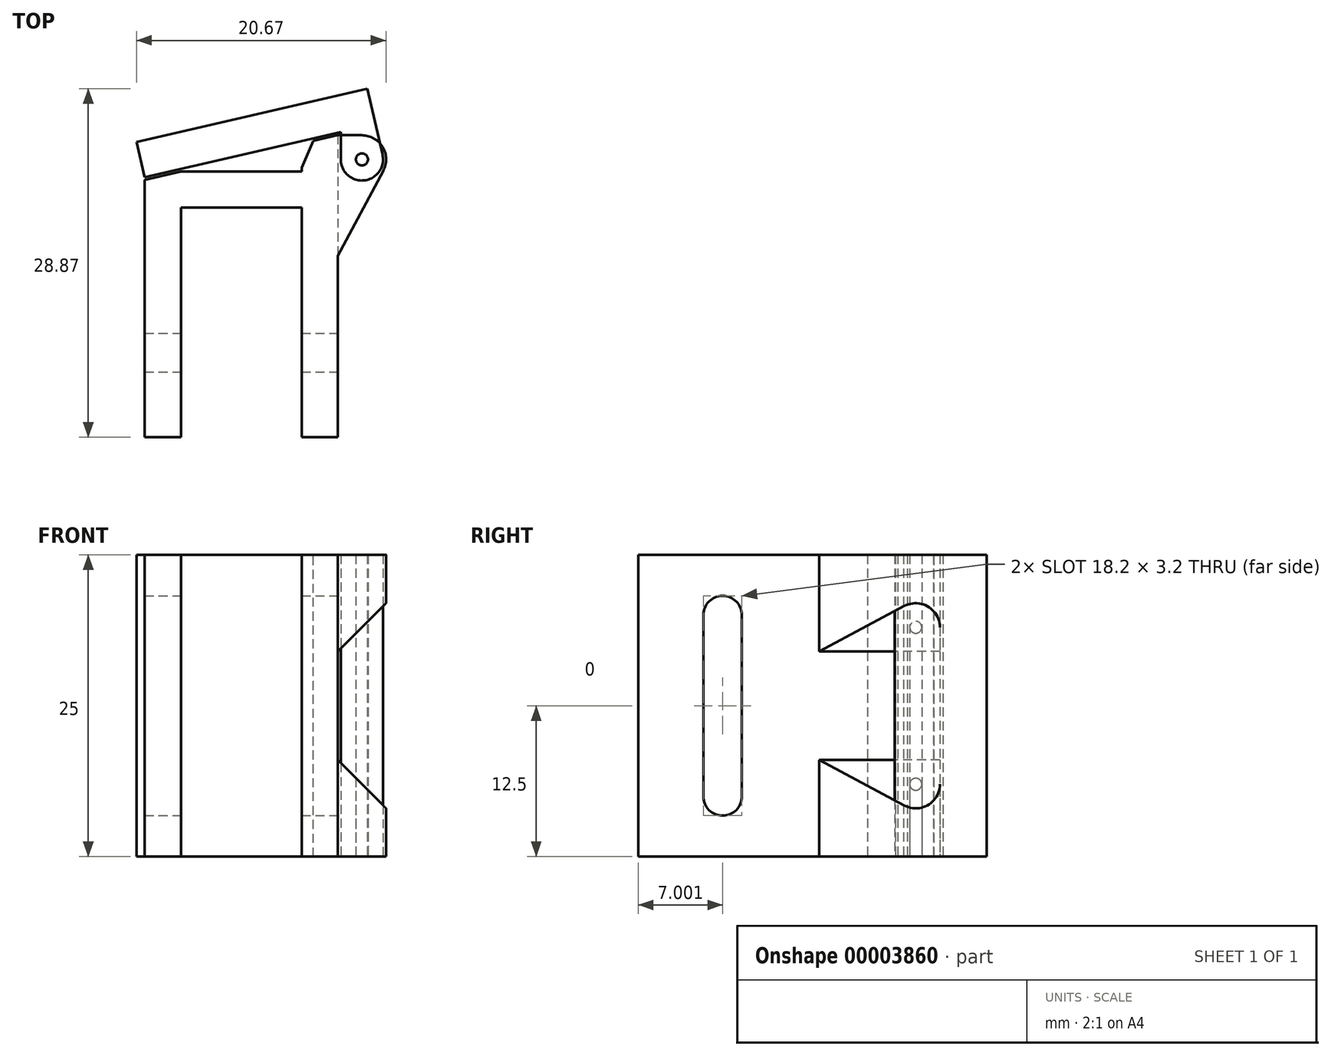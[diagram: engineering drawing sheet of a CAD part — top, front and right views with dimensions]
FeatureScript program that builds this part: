
annotation { "Feature Type Name" : "Feature", "Feature Type Description" : "" }
export const myFeature = defineFeature(function(context is Context, id is Id, definition is map)
    precondition{}
    {
        {
            var Q0;
            Q0=qCreatedBy(makeId("Top.planeOp"),FACE);
            var sketch = newSketch(context, id + "F0", { "sketchPlane" : qUnion([Q0])});
            skLineSegment(sketch, "E0", {"start": v(-92.53, 19.33) * mm, "end": v(-92.53, -5.67) * mm});
            skLineSegment(sketch, "E1", {"start": v(-92.53, -5.67) * mm, "end": v(-95.53, -5.67) * mm});
            skLineSegment(sketch, "E2", {"start": v(-95.53, -5.67) * mm, "end": v(-95.53, 13.33) * mm});
            skLineSegment(sketch, "E3", {"start": v(-95.53, 13.33) * mm, "end": v(-105.53, 13.33) * mm});
            skLineSegment(sketch, "E4", {"start": v(-105.53, 13.33) * mm, "end": v(-105.53, -5.67) * mm});
            skLineSegment(sketch, "E5", {"start": v(-105.53, -5.67) * mm, "end": v(-108.53, -5.67) * mm});
            skLineSegment(sketch, "E6", {"start": v(-108.53, -5.67) * mm, "end": v(-108.53, 15.64) * mm});
            skLineSegment(sketch, "E7", {"start": v(-105.53, 16.33) * mm, "end": v(-95.53, 16.33) * mm});
            skLineSegment(sketch, "E8", {"start": v(-95.53, 16.33) * mm, "end": v(-95.53, 18.64) * mm});
            skLineSegment(sketch, "E9", {"start": v(-92.53, 19.33) * mm, "end": v(-95.53, 18.64) * mm, "construction": true});
            skLineSegment(sketch, "E10", {"start": v(-105.53, 16.33) * mm, "end": v(-108.53, 15.64) * mm, "construction": true});
            skLineSegment(sketch, "E11", {"start": v(-108.53, 15.64) * mm, "end": v(-105.53, 16.33) * mm});
            skLineSegment(sketch, "E12", {"start": v(-92.53, 19.33) * mm, "end": v(-95.53, 18.64) * mm});
            skSolve(sketch);
        }
        {
            var Q0;
            Q0=makeQuery(id+"F0.imprint","IMPRINT",FACE,{"disambiguationData":[TD([[makeQuery(id+"F0.imprint","IMPRINT",EDGE,{"derivedFrom":sQuery(id+"F0.wireOp",EDGE,"E0")}),-1.0]])]});
            extrude(context, id + "F1", {"entities" : qUnion([Q0]), "depth" : 25 * mm});
        }
        {
            var Q0;
            Q0=makeQuery(id+"F1.opExtrude","CAP_FACE",FACE,{"disambiguationData":[OSD([sQuery(id+"F0.wireOp",EDGE,"E0"),sQuery(id+"F0.wireOp",EDGE,"E1"),sQuery(id+"F0.wireOp",EDGE,"E2"),sQuery(id+"F0.wireOp",EDGE,"E3"),sQuery(id+"F0.wireOp",EDGE,"E4"),sQuery(id+"F0.wireOp",EDGE,"E5"),sQuery(id+"F0.wireOp",EDGE,"E6"),sQuery(id+"F0.wireOp",EDGE,"E7"),sQuery(id+"F0.wireOp",EDGE,"E8"),sQuery(id+"F0.wireOp",EDGE,"E11"),sQuery(id+"F0.wireOp",EDGE,"E12")])],"isStart":true});
            var sketch = newSketch(context, id + "F2", { "sketchPlane" : qUnion([Q0])});
            skCircle(sketch, "E13", {"center": v(-90.53, -17.33) * mm, "radius": 0.5 * mm});
            skArc(sketch, "E14", {"start": v(-90.53, -19.33) * mm, "mid": v(-88.81, -18.36) * mm, "end": v(-88.76, -16.39) * mm});
            skLineSegment(sketch, "E15", {"start": v(-92.53, -19.33) * mm, "end": v(-90.53, -19.33) * mm});
            skLineSegment(sketch, "E16", {"start": v(-92.53, -9.33) * mm, "end": v(-88.76, -16.39) * mm});
            skLineSegment(sketch, "E17", {"start": v(-92.53, -19.33) * mm, "end": v(-92.53, -9.33) * mm});
            skSolve(sketch);
        }
        {
            var Q0;
            Q0=makeQuery(id+"F2.imprint","IMPRINT",FACE,{"disambiguationData":[TD([[makeQuery(id+"F2.imprint","IMPRINT",EDGE,{"derivedFrom":sQuery(id+"F2.wireOp",EDGE,"E13")}),-1.0]])]});
            extrude(context, id + "F3", {"entities" : qUnion([Q0]), "operationType" : NewBodyOperationType.ADD, "oppositeDirection" : true, "depth" : 25 * mm});
        }
        {
            var Q0;
            Q0=makeQuery(id+"F1.opExtrude","SWEPT_FACE",FACE,{"disambiguationData":[OSD([sQuery(id+"F0.wireOp",EDGE,"E1")])]});
            var sketch = newSketch(context, id + "F4", { "sketchPlane" : qUnion([Q0])});
            skLineSegment(sketch, "E18", {"start": v(-92.53, 17) * mm, "end": v(-82.19, 27.34) * mm});
            skLineSegment(sketch, "E19", {"start": v(-82.19, 27.34) * mm, "end": v(-82.19, -2.34) * mm});
            skLineSegment(sketch, "E20", {"start": v(-82.19, -2.34) * mm, "end": v(-92.53, 8) * mm});
            skLineSegment(sketch, "E21", {"start": v(-92.53, 8) * mm, "end": v(-92.53, 17) * mm});
            skSolve(sketch);
        }
        {
            var Q0;
            Q0=makeQuery(id+"F4.imprint","IMPRINT",FACE,{"disambiguationData":[TD([[makeQuery(id+"F4.imprint","IMPRINT",EDGE,{"derivedFrom":sQuery(id+"F4.wireOp",EDGE,"E18")}),-1.0]])]});
            extrude(context, id + "F5", {"entities" : qUnion([Q0]), "operationType" : NewBodyOperationType.REMOVE, "oppositeDirection" : true, "depth" : 30 * mm});
        }
        {
            var Q0;
            Q0=makeQuery(id+"F5.boolean.opBoolean","MERGE",FACE,{"derivedFrom":[makeQuery(id+"F1.opExtrude","SWEPT_FACE",FACE,{"disambiguationData":[OSD([sQuery(id+"F0.wireOp",EDGE,"E0")])]}),makeQuery(id+"F5.opExtrude","SWEPT_FACE",FACE,{"disambiguationData":[OSD([sQuery(id+"F4.wireOp",EDGE,"E21")])]})]});
            var sketch = newSketch(context, id + "F6", { "sketchPlane" : qUnion([Q0])});
            skArc(sketch, "E22", {"start": v(2.93, 20) * mm, "mid": v(1.33, 21.6) * mm, "end": v(-0.27, 20) * mm});
            skArc(sketch, "E23", {"start": v(-0.27, 5) * mm, "mid": v(1.33, 3.4) * mm, "end": v(2.93, 5) * mm});
            skLineSegment(sketch, "E24.right", {"start": v(2.93, 20) * mm, "end": v(2.93, 5) * mm});
            skLineSegment(sketch, "E25.right", {"start": v(-0.27, 5) * mm, "end": v(-0.27, 20) * mm});
            skSolve(sketch);
        }
        {
            var Q0;
            Q0=makeQuery(id+"F6.imprint","IMPRINT",FACE,{"disambiguationData":[TD([[makeQuery(id+"F6.imprint","IMPRINT",EDGE,{"derivedFrom":sQuery(id+"F6.wireOp",EDGE,"E22")}),1.0]])]});
            extrude(context, id + "F7", {"entities" : qUnion([Q0]), "operationType" : NewBodyOperationType.REMOVE, "oppositeDirection" : true, "depth" : 25 * mm});
        }
        {
            var Q0;
            Q0=makeQuery(id+"F1.opExtrude","SWEPT_EDGE",EDGE,{"disambiguationData":[OSD([sQuery(id+"F0.wireOp",EDGE,"E8"),sQuery(id+"F0.wireOp",EDGE,"E12")])]});
            chamfer(context, id + "F8", {"entities" : qUnion([Q0]), "chamferType" : ChamferType.TWO_OFFSETS, "width1" : 2 * mm, "oppositeDirection" : false, "width2" : 1 * mm, "tangentPropagation" : true});
        }
        {
            var Q0;
            Q0=makeQuery(id+"F3.boolean.opBoolean","MERGE",FACE,{"derivedFrom":[makeQuery(id+"F1.opExtrude","CAP_FACE",FACE,{"disambiguationData":[OSD([sQuery(id+"F0.wireOp",EDGE,"E0"),sQuery(id+"F0.wireOp",EDGE,"E1"),sQuery(id+"F0.wireOp",EDGE,"E2"),sQuery(id+"F0.wireOp",EDGE,"E3"),sQuery(id+"F0.wireOp",EDGE,"E4"),sQuery(id+"F0.wireOp",EDGE,"E5"),sQuery(id+"F0.wireOp",EDGE,"E6"),sQuery(id+"F0.wireOp",EDGE,"E7"),sQuery(id+"F0.wireOp",EDGE,"E8"),sQuery(id+"F0.wireOp",EDGE,"E11"),sQuery(id+"F0.wireOp",EDGE,"E12")])],"isStart":true}),makeQuery(id+"F3.opExtrude","CAP_FACE",FACE,{"disambiguationData":[OSD([sQuery(id+"F2.wireOp",EDGE,"E13"),sQuery(id+"F2.wireOp",EDGE,"E14"),sQuery(id+"F2.wireOp",EDGE,"E15"),sQuery(id+"F2.wireOp",EDGE,"E16"),sQuery(id+"F2.wireOp",EDGE,"E17")])],"isStart":true})]});
            var sketch = newSketch(context, id + "F9", { "sketchPlane" : qUnion([Q0])});
            skCircle(sketch, "E26", {"center": v(-90.53, -17.33) * mm, "radius": 0.5 * mm});
            skCircle(sketch, "E27", {"center": v(-90.53, -17.33) * mm, "radius": 1.75 * mm});
            skLineSegment(sketch, "E28", {"start": v(-90.53, -17.33) * mm, "end": v(-80.71, -17.33) * mm, "construction": true});
            skLineSegment(sketch, "E29", {"start": v(-90.53, -17.33) * mm, "end": v(-93.59, -17.33) * mm, "construction": true});
            skLineSegment(sketch, "E30", {"start": v(-92.28, -17.33) * mm, "end": v(-92.28, -19.6) * mm});
            skLineSegment(sketch, "E31", {"start": v(-92.28, -19.6) * mm, "end": v(-108.53, -15.84) * mm});
            skLineSegment(sketch, "E32", {"start": v(-108.53, -15.84) * mm, "end": v(-109.2, -18.79) * mm});
            skLineSegment(sketch, "E33", {"start": v(-90.08, -23.2) * mm, "end": v(-88.82, -17.72) * mm});
            skLineSegment(sketch, "E34", {"start": v(-90.53, -17.33) * mm, "end": v(-90.04, -17.44) * mm});
            skLineSegment(sketch, "E35", {"start": v(-109.2, -18.79) * mm, "end": v(-90.08, -23.2) * mm});
            skSolve(sketch);
        }
        {
            var Q0;
            Q0 = qSketchRegion(id + "F9", true);
            extrude(context, id + "F10", {"entities" : qUnion([Q0]), "oppositeDirection" : true, "depth" : 25 * mm});
        }
    });
